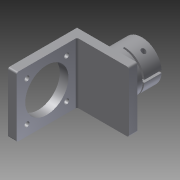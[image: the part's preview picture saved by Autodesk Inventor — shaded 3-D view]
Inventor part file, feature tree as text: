
AUTODESK INVENTOR PART (.ipt)
format: ipt  version: 2011 (Build 150239000, 239)  size: 205,312 bytes
history: native  units: mm
features: extrude x10, sketch x10, plane x5, fillet x2
ambient origin geometry x8: Origin, YZ Plane, XZ Plane, XY Plane, X Axis, Y Axis, Z Axis, Center Point
bodies: Volumenkörper1 (feature_tree)
feature tree (27):
  plane  "Arbeitsebene10"
  extrude  "Achshalter"  Depth=20.0mm TaperAngle=0.0deg
  plane  "Arbeitsebene11"
  extrude  "Extrusion11"  Depth=2.2mm
  plane  "Arbeitsebene2"
  extrude  "Extrusion12"  Depth=1.0mm TaperAngle=0.0deg
  plane  "Arbeitsebene16"
  extrude  "Extrusion13"  Depth=2.5mm
  plane  "Arbeitsebene17"
  extrude  "Extrusion14"  Depth=35.0mm
  extrude  "Extrusion17"  Depth=17.5mm
  extrude  "Extrusion18"  Depth=5.0mm TaperAngle=0.0deg
  fillet  "Rundung14"  Radius=35.0mm
  fillet  "Rundung15"  Radius=35.0mm
  extrude  "Extrusion19"  Depth=1.0mm
  extrude  "Extrusion20"  Depth=25.0mm
  extrude  "Extrusion21"  Depth=10.0mm TaperAngle=0.0deg
  sketch  "Skizze7"  dims[d32=23.0mm d33=20.0mm d34=0.0mm]
  sketch  "Skizze16"  dims[d54=5.2mm d55=2.2mm]
  sketch  "Skizze17"  dims[d56=18.0mm d57=0.0mm d59=1.0mm d60=0.0mm]
  sketch  "Skizze18"  dims[d63=1.0mm d64=0.5mm d65=0.0mm d66=0.0mm d67=2.5mm]
  sketch  "Skizze19"  dims[d68=35.0mm d69=0.0mm d90=35.0mm]
  sketch  "Skizze24"  dims[d91=35.0mm d92=17.5mm]
  sketch  "Skizze25"  dims[d93=17.5mm d94=5.0mm d95=0.0mm d96=35.0mm d97=35.0mm]
  sketch  "Skizze26"  dims[d98=5.0mm d99=0.0mm d100=1.0mm]
  sketch  "Skizze27"  dims[d101=1.0mm d102=25.0mm]
  sketch  "Skizze28"  dims[d103=17.5mm d104=10.0mm d105=0.0mm d106=2.8mm d107=2.8mm d108=2.8mm d109=2.8mm d110=23.0mm d111=23.0mm d112=23.0mm d113=23.0mm d114=10.0mm d115=0.0mm d116=5.0mm d117=5.0mm d118=5.0mm d119=5.0mm d120=2.0mm d121=0.0mm]
